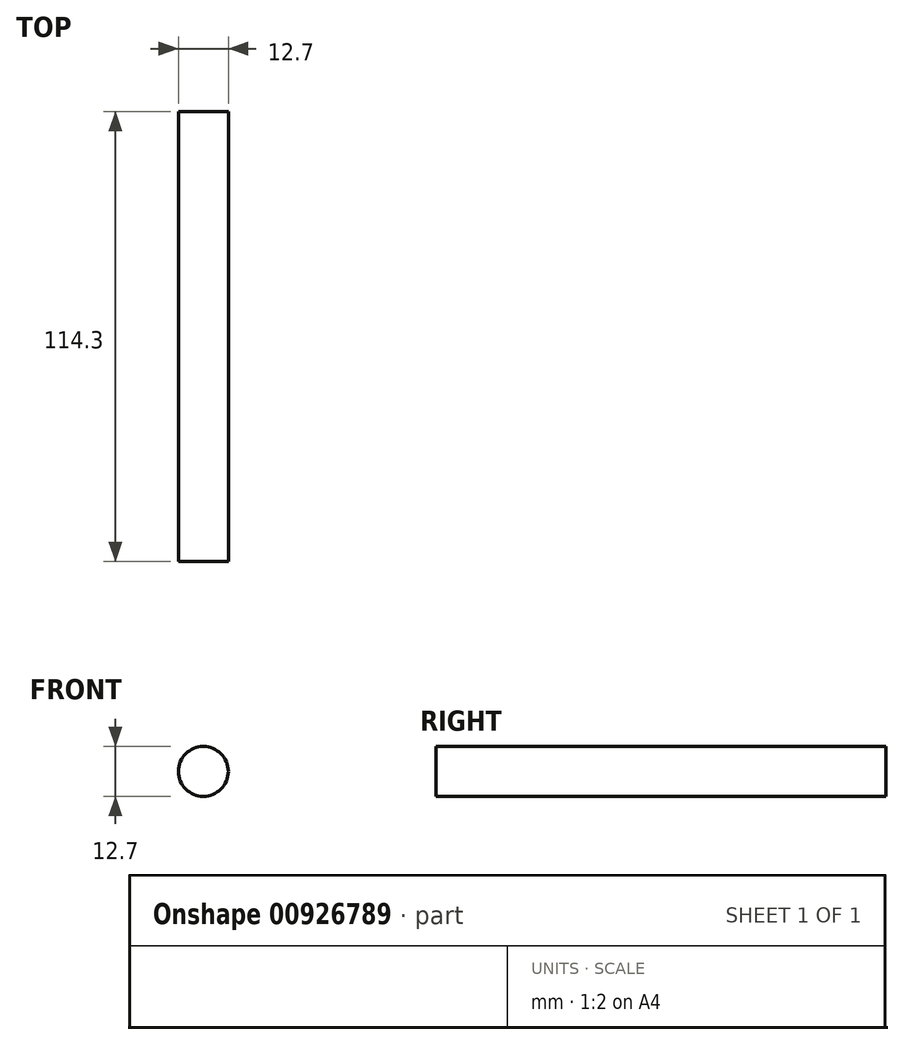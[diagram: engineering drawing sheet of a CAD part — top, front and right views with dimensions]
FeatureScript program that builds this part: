
annotation { "Feature Type Name" : "Feature", "Feature Type Description" : "" }
export const myFeature = defineFeature(function(context is Context, id is Id, definition is map)
    precondition{}
    {
        {
            var Q0;
            Q0=qCreatedBy(makeId("Front.planeOp"),FACE);
            var sketch = newSketch(context, id + "F0", { "sketchPlane" : qUnion([Q0])});
            skCircle(sketch, "E0", {"center": v(0, 0) * mm, "radius": 6.35 * mm});
            skSolve(sketch);
        }
        {
            var Q0;
            Q0=makeQuery(id+"F0.imprint","IMPRINT",FACE,{"disambiguationData":[TD([[makeQuery(id+"F0.imprint","IMPRINT",EDGE,{"derivedFrom":sQuery(id+"F0.wireOp",EDGE,"E0")}),1.0]])]});
            extrude(context, id + "F1", {"entities" : qUnion([Q0]), "depth" : 114.3 * mm, "offsetDistance" : 25.4 * mm});
        }
    });
